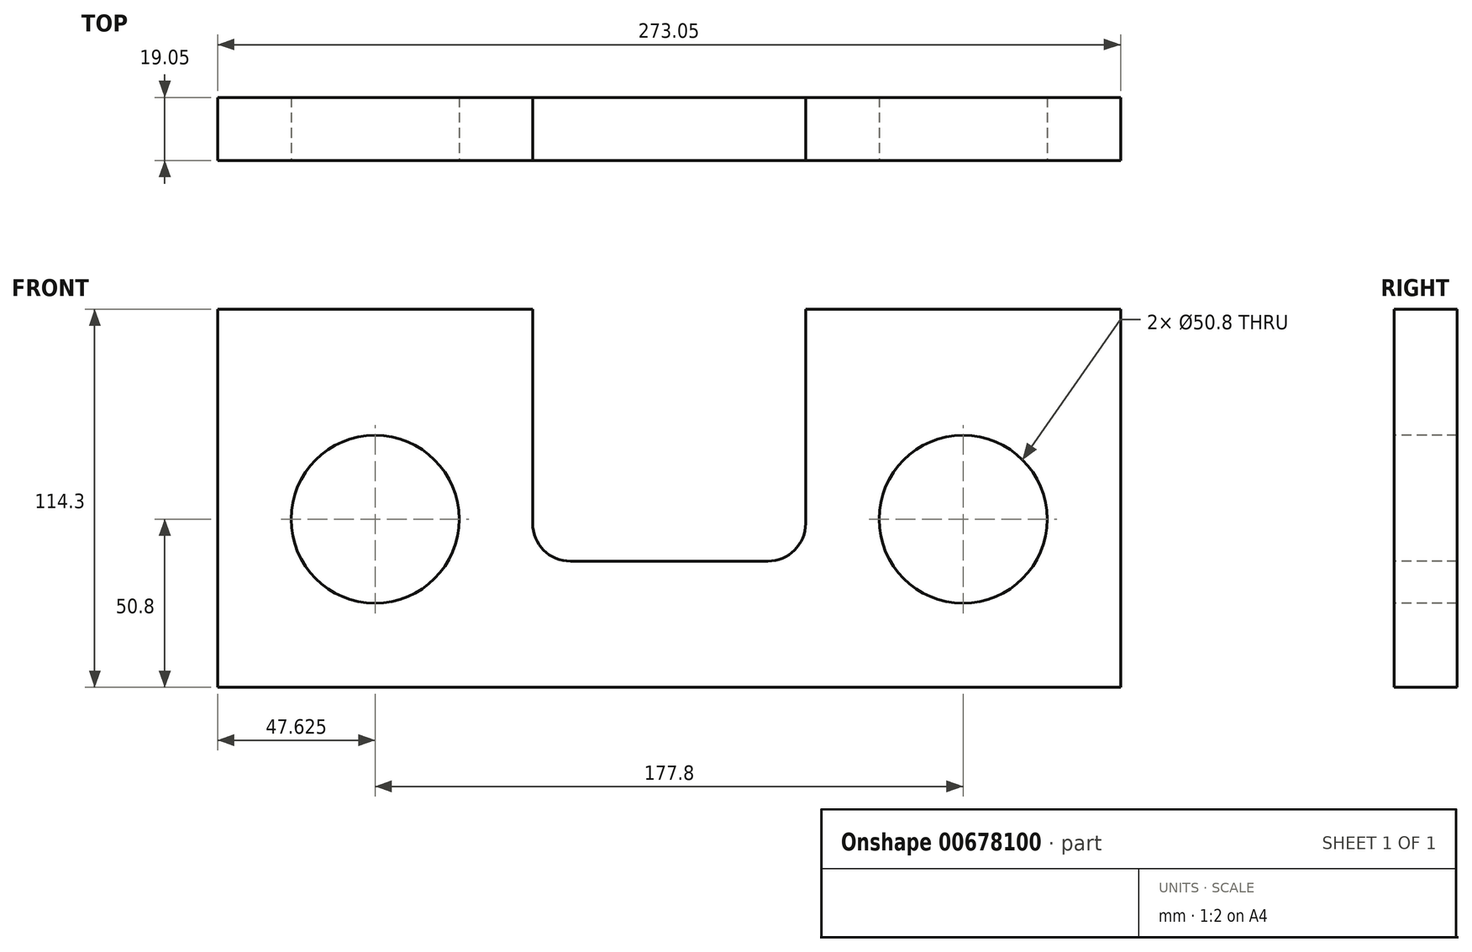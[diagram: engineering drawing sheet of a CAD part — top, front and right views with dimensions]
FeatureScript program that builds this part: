
annotation { "Feature Type Name" : "Feature", "Feature Type Description" : "" }
export const myFeature = defineFeature(function(context is Context, id is Id, definition is map)
    precondition{}
    {
        {
            var Q0;
            Q0=qCreatedBy(makeId("Front.planeOp"),FACE);
            var sketch = newSketch(context, id + "F0", { "sketchPlane" : qUnion([Q0])});
            skLineSegment(sketch, "E0.bottom", {"start": v(0, 0) * mm, "end": v(273.05, 0) * mm});
            skLineSegment(sketch, "E0.top", {"start": v(0, 114.3) * mm, "end": v(273.05, 114.3) * mm});
            skLineSegment(sketch, "E0.left", {"start": v(0, 0) * mm, "end": v(0, 114.3) * mm});
            skLineSegment(sketch, "E0.right", {"start": v(273.05, 0) * mm, "end": v(273.05, 114.3) * mm});
            skSolve(sketch);
        }
        {
            var Q0;
            Q0=makeQuery(id+"F0.imprint","IMPRINT",FACE,{"disambiguationData":[TD([[makeQuery(id+"F0.imprint","IMPRINT",EDGE,{"derivedFrom":sQuery(id+"F0.wireOp",EDGE,"E0.bottom")}),1.0]])]});
            extrude(context, id + "F1", {"entities" : qUnion([Q0]), "depth" : 19.05 * mm, "offsetDistance" : 25.4 * mm});
        }
        {
            var Q0;
            Q0=makeQuery(id+"F1.opExtrude","CAP_FACE",FACE,{"disambiguationData":[OSD([sQuery(id+"F0.wireOp",EDGE,"E0.bottom"),sQuery(id+"F0.wireOp",EDGE,"E0.top"),sQuery(id+"F0.wireOp",EDGE,"E0.left"),sQuery(id+"F0.wireOp",EDGE,"E0.right")])],"isStart":false});
            var sketch = newSketch(context, id + "F2", { "sketchPlane" : qUnion([Q0])});
            skCircle(sketch, "E1", {"center": v(47.63, 50.8) * mm, "radius": 25.4 * mm});
            skCircle(sketch, "E2", {"center": v(225.43, 50.8) * mm, "radius": 25.4 * mm});
            skSolve(sketch);
        }
        {
            var Q0;
            Q0=makeQuery(id+"F2.imprint","IMPRINT",FACE,{"disambiguationData":[TD([[makeQuery(id+"F2.imprint","IMPRINT",EDGE,{"derivedFrom":sQuery(id+"F2.wireOp",EDGE,"E1")}),1.0]])]});
            var Q1;
            Q1=makeQuery(id+"F2.imprint","IMPRINT",FACE,{"disambiguationData":[TD([[makeQuery(id+"F2.imprint","IMPRINT",EDGE,{"derivedFrom":sQuery(id+"F2.wireOp",EDGE,"E2")}),1.0]])]});
            extrude(context, id + "F3", {"entities" : qUnion([Q0, Q1]), "operationType" : NewBodyOperationType.REMOVE, "oppositeDirection" : true, "depth" : 25.4 * mm, "offsetDistance" : 25.4 * mm});
        }
        {
            var Q0;
            Q0=makeQuery(id+"F1.opExtrude","CAP_FACE",FACE,{"disambiguationData":[OSD([sQuery(id+"F0.wireOp",EDGE,"E0.bottom"),sQuery(id+"F0.wireOp",EDGE,"E0.top"),sQuery(id+"F0.wireOp",EDGE,"E0.left"),sQuery(id+"F0.wireOp",EDGE,"E0.right")])],"isStart":false});
            var sketch = newSketch(context, id + "F4", { "sketchPlane" : qUnion([Q0])});
            skLineSegment(sketch, "E3", {"start": v(95.25, 114.3) * mm, "end": v(95.25, 49.53) * mm});
            skLineSegment(sketch, "E4", {"start": v(106.68, 38.1) * mm, "end": v(166.37, 38.1) * mm});
            skLineSegment(sketch, "E5", {"start": v(177.8, 49.53) * mm, "end": v(177.8, 114.3) * mm});
            skPoint(sketch, "E6.visualSharp", {"position": v(95.25, 38.1) * mm});
            skArc(sketch, "E6.filletArc", {"start": v(95.25, 49.53) * mm, "mid": v(98.6, 41.45) * mm, "end": v(106.68, 38.1) * mm});
            skPoint(sketch, "E7.visualSharp", {"position": v(177.8, 38.1) * mm});
            skArc(sketch, "E7.filletArc", {"start": v(166.37, 38.1) * mm, "mid": v(174.45, 41.45) * mm, "end": v(177.8, 49.53) * mm});
            skSolve(sketch);
        }
        {
            var Q0;
            {var subQ1=sQuery(id+"F4.wireOp",EDGE,"E3");Q0=makeQuery(id+"F4.imprint","IMPRINT",FACE,{"disambiguationData":[TD([[makeQuery(id+"F4.imprint","IMPRINT",EDGE,{"derivedFrom":subQ1}),1.0]])]});}
            extrude(context, id + "F5", {"entities" : qUnion([Q0]), "operationType" : NewBodyOperationType.REMOVE, "oppositeDirection" : true, "depth" : 25.4 * mm, "offsetDistance" : 25.4 * mm});
        }
    });
